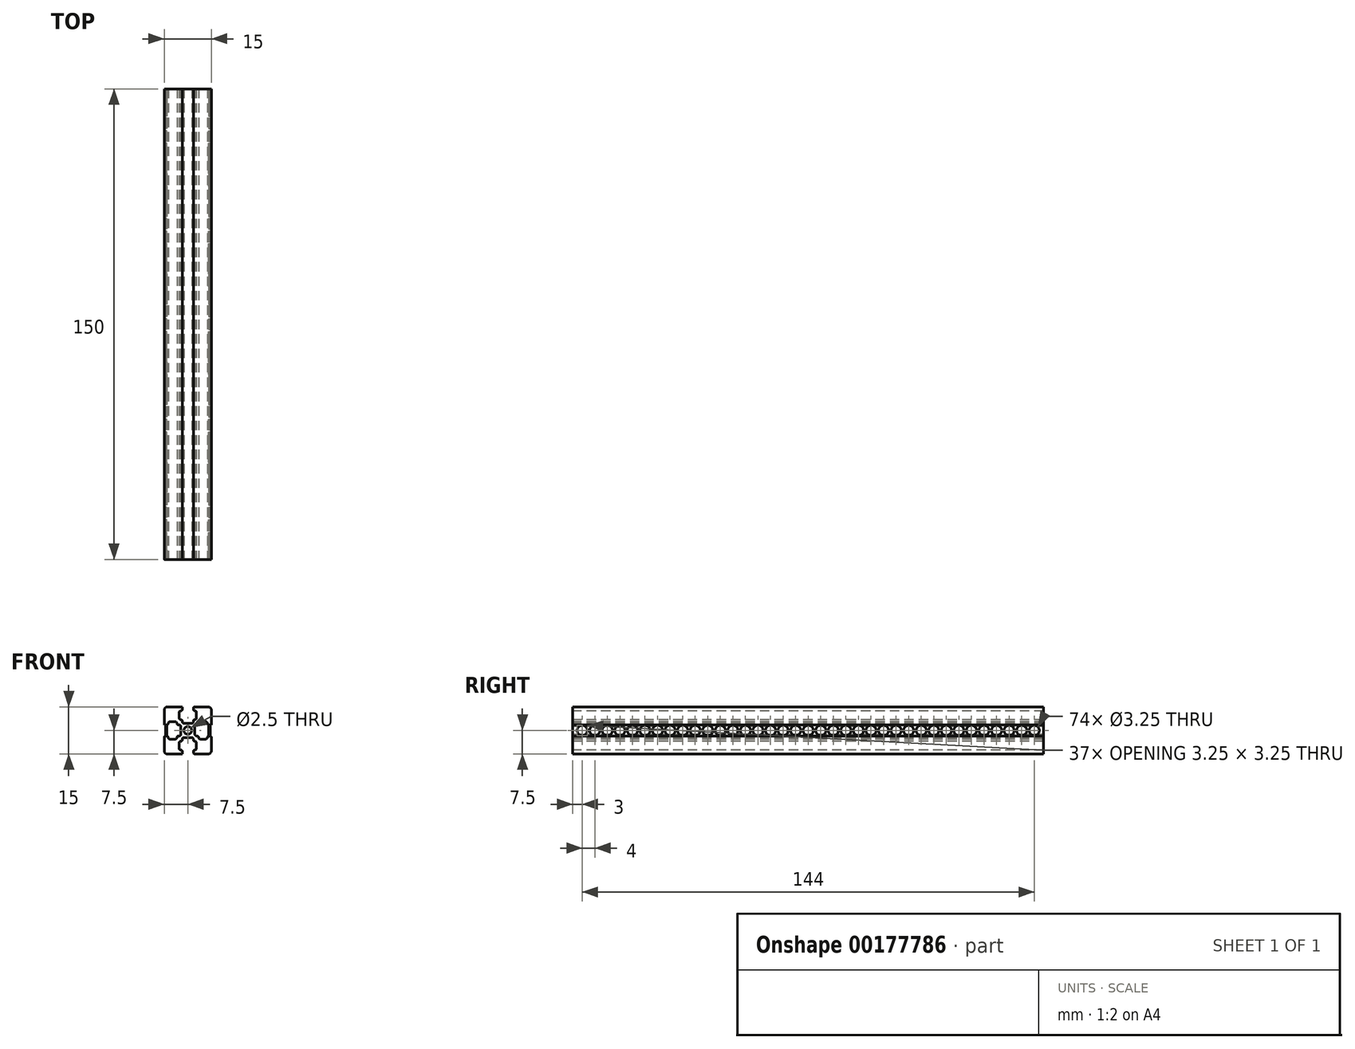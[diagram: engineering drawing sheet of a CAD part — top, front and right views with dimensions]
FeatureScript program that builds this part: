
annotation { "Feature Type Name" : "Feature", "Feature Type Description" : "" }
export const myFeature = defineFeature(function(context is Context, id is Id, definition is map)
    precondition{}
    {
        {
            var Q0;
            Q0=qCreatedBy(makeId("Front.planeOp"),FACE);
            var sketch = newSketch(context, id + "F0", { "sketchPlane" : qUnion([Q0])});
            skLineSegment(sketch, "E0.bottom", {"start": v(-6.5, 7.5) * mm, "end": v(6.5, 7.5) * mm});
            skLineSegment(sketch, "E0.top", {"start": v(-6.5, -7.5) * mm, "end": v(6.5, -7.5) * mm});
            skLineSegment(sketch, "E0.left", {"start": v(-7.5, 6.5) * mm, "end": v(-7.5, -6.5) * mm});
            skLineSegment(sketch, "E0.right", {"start": v(7.5, 6.5) * mm, "end": v(7.5, -6.5) * mm});
            skPoint(sketch, "E1.visualSharp", {"position": v(-7.5, 7.5) * mm});
            skArc(sketch, "E1.filletArc", {"start": v(-6.5, 7.5) * mm, "mid": v(-7.2, 7.2) * mm, "end": v(-7.5, 6.5) * mm});
            skPoint(sketch, "E2.visualSharp", {"position": v(7.5, 7.5) * mm});
            skArc(sketch, "E2.filletArc", {"start": v(7.5, 6.5) * mm, "mid": v(7.2, 7.2) * mm, "end": v(6.5, 7.5) * mm});
            skPoint(sketch, "E3.visualSharp", {"position": v(7.5, -7.5) * mm});
            skArc(sketch, "E3.filletArc", {"start": v(6.5, -7.5) * mm, "mid": v(7.2, -7.2) * mm, "end": v(7.5, -6.5) * mm});
            skPoint(sketch, "E4.visualSharp", {"position": v(-7.5, -7.5) * mm});
            skArc(sketch, "E4.filletArc", {"start": v(-7.5, -6.5) * mm, "mid": v(-7.2, -7.2) * mm, "end": v(-6.5, -7.5) * mm});
            skSolve(sketch);
        }
        {
            var Q0;
            Q0 = qSketchRegion(id + "F0", true);
            extrude(context, id + "F1", {"entities" : qUnion([Q0]), "depth" : 150 * mm});
        }
        {
            var Q0;
            Q0=makeQuery(id+"F1.opExtrude","CAP_FACE",FACE,{"disambiguationData":[OSD([sQuery(id+"F0.wireOp",EDGE,"E0.bottom"),sQuery(id+"F0.wireOp",EDGE,"E0.top"),sQuery(id+"F0.wireOp",EDGE,"E0.left"),sQuery(id+"F0.wireOp",EDGE,"E0.right")])],"isStart":false});
            var sketch = newSketch(context, id + "F2", { "sketchPlane" : qUnion([Q0])});
            skLineSegment(sketch, "E5.top", {"start": v(-1.25, -2.25) * mm, "end": v(1.25, -2.25) * mm});
            skLineSegment(sketch, "E5.left", {"start": v(-1.75, -7.5) * mm, "end": v(-1.75, -6.75) * mm});
            skLineSegment(sketch, "E5.right", {"start": v(1.75, -7.5) * mm, "end": v(1.75, -6.75) * mm});
            skLineSegment(sketch, "E6.bottom", {"start": v(-2.25, -3.45) * mm, "end": v(-2.25, -3.45) * mm});
            skLineSegment(sketch, "E6.top", {"start": v(-2.25, -6.25) * mm, "end": v(-2.25, -6.25) * mm});
            skLineSegment(sketch, "E6.left", {"start": v(-2.75, -3.95) * mm, "end": v(-2.75, -5.75) * mm});
            skLineSegment(sketch, "E6.right", {"start": v(2.75, -3.95) * mm, "end": v(2.75, -5.75) * mm});
            skLineSegment(sketch, "E7.trimOffspring", {"start": v(-1.75, -2.95) * mm, "end": v(-1.75, -2.75) * mm});
            skLineSegment(sketch, "E8.trimOffspring", {"start": v(2.25, -3.45) * mm, "end": v(2.25, -3.45) * mm});
            skLineSegment(sketch, "E9.trimOffspring", {"start": v(1.75, -2.95) * mm, "end": v(1.75, -2.75) * mm});
            skLineSegment(sketch, "E10.trimOffspring", {"start": v(2.25, -6.25) * mm, "end": v(2.25, -6.25) * mm});
            skLineSegment(sketch, "E11.MirrorCS", {"start": v(-1.25, 2.25) * mm, "end": v(1.25, 2.25) * mm});
            skLineSegment(sketch, "E12.MirrorCS", {"start": v(-1.75, 2.95) * mm, "end": v(-1.75, 2.75) * mm});
            skLineSegment(sketch, "E13.MirrorCS", {"start": v(1.75, 2.95) * mm, "end": v(1.75, 2.75) * mm});
            skLineSegment(sketch, "E14.MirrorCS", {"start": v(2.25, 3.45) * mm, "end": v(2.25, 3.45) * mm});
            skLineSegment(sketch, "E15.MirrorCS", {"start": v(-2.25, 3.45) * mm, "end": v(-2.25, 3.45) * mm});
            skLineSegment(sketch, "E16.MirrorCS", {"start": v(-2.75, 3.95) * mm, "end": v(-2.75, 5.75) * mm});
            skLineSegment(sketch, "E17.MirrorCS", {"start": v(2.75, 3.95) * mm, "end": v(2.75, 5.75) * mm});
            skLineSegment(sketch, "E18.MirrorCS", {"start": v(2.25, 6.25) * mm, "end": v(2.25, 6.25) * mm});
            skLineSegment(sketch, "E19.MirrorCS", {"start": v(-2.25, 6.25) * mm, "end": v(-2.25, 6.25) * mm});
            skLineSegment(sketch, "E20.MirrorCS", {"start": v(-1.75, 7.5) * mm, "end": v(-1.75, 6.75) * mm});
            skLineSegment(sketch, "E21.MirrorCS", {"start": v(1.75, 7.5) * mm, "end": v(1.75, 6.75) * mm});
            skLineSegment(sketch, "E22", {"start": v(-1.75, 7.5) * mm, "end": v(1.75, 7.5) * mm});
            skLineSegment(sketch, "E23", {"start": v(-1.75, -7.5) * mm, "end": v(1.75, -7.5) * mm});
            skPoint(sketch, "E24.visualSharp", {"position": v(-1.75, -6.25) * mm});
            skArc(sketch, "E24.filletArc", {"start": v(-1.75, -6.75) * mm, "mid": v(-1.9, -6.4) * mm, "end": v(-2.25, -6.25) * mm});
            skPoint(sketch, "E25.visualSharp", {"position": v(-2.75, -6.25) * mm});
            skArc(sketch, "E25.filletArc", {"start": v(-2.75, -5.75) * mm, "mid": v(-2.6, -6.1) * mm, "end": v(-2.25, -6.25) * mm});
            skPoint(sketch, "E26.visualSharp", {"position": v(-2.75, -3.45) * mm});
            skArc(sketch, "E26.filletArc", {"start": v(-2.25, -3.45) * mm, "mid": v(-2.6, -3.6) * mm, "end": v(-2.75, -3.95) * mm});
            skPoint(sketch, "E27.visualSharp", {"position": v(-1.75, -3.45) * mm});
            skArc(sketch, "E27.filletArc", {"start": v(-2.25, -3.45) * mm, "mid": v(-1.9, -3.3) * mm, "end": v(-1.75, -2.95) * mm});
            skPoint(sketch, "E28.visualSharp", {"position": v(1.75, -6.25) * mm});
            skArc(sketch, "E28.filletArc", {"start": v(2.25, -6.25) * mm, "mid": v(1.9, -6.4) * mm, "end": v(1.75, -6.75) * mm});
            skPoint(sketch, "E29.visualSharp", {"position": v(2.75, -6.25) * mm});
            skArc(sketch, "E29.filletArc", {"start": v(2.25, -6.25) * mm, "mid": v(2.6, -6.1) * mm, "end": v(2.75, -5.75) * mm});
            skPoint(sketch, "E30.visualSharp", {"position": v(2.75, -3.45) * mm});
            skArc(sketch, "E30.filletArc", {"start": v(2.75, -3.95) * mm, "mid": v(2.6, -3.6) * mm, "end": v(2.25, -3.45) * mm});
            skPoint(sketch, "E31.visualSharp", {"position": v(1.75, -3.45) * mm});
            skArc(sketch, "E31.filletArc", {"start": v(1.75, -2.95) * mm, "mid": v(1.9, -3.3) * mm, "end": v(2.25, -3.45) * mm});
            skPoint(sketch, "E32.visualSharp", {"position": v(1.75, -2.25) * mm});
            skArc(sketch, "E32.filletArc", {"start": v(1.75, -2.75) * mm, "mid": v(1.6, -2.4) * mm, "end": v(1.25, -2.25) * mm});
            skPoint(sketch, "E33.visualSharp", {"position": v(-1.75, -2.25) * mm});
            skArc(sketch, "E33.filletArc", {"start": v(-1.25, -2.25) * mm, "mid": v(-1.6, -2.4) * mm, "end": v(-1.75, -2.75) * mm});
            skPoint(sketch, "E34.visualSharp", {"position": v(-1.75, 2.25) * mm});
            skArc(sketch, "E34.filletArc", {"start": v(-1.75, 2.75) * mm, "mid": v(-1.6, 2.4) * mm, "end": v(-1.25, 2.25) * mm});
            skPoint(sketch, "E35.visualSharp", {"position": v(1.75, 2.25) * mm});
            skArc(sketch, "E35.filletArc", {"start": v(1.25, 2.25) * mm, "mid": v(1.6, 2.4) * mm, "end": v(1.75, 2.75) * mm});
            skPoint(sketch, "E36.visualSharp", {"position": v(1.75, 3.45) * mm});
            skArc(sketch, "E36.filletArc", {"start": v(2.25, 3.45) * mm, "mid": v(1.9, 3.3) * mm, "end": v(1.75, 2.95) * mm});
            skPoint(sketch, "E37.visualSharp", {"position": v(2.75, 6.25) * mm});
            skArc(sketch, "E37.filletArc", {"start": v(2.75, 5.75) * mm, "mid": v(2.6, 6.1) * mm, "end": v(2.25, 6.25) * mm});
            skPoint(sketch, "E38.visualSharp", {"position": v(2.75, 3.45) * mm});
            skArc(sketch, "E38.filletArc", {"start": v(2.25, 3.45) * mm, "mid": v(2.6, 3.6) * mm, "end": v(2.75, 3.95) * mm});
            skPoint(sketch, "E39.visualSharp", {"position": v(1.75, 6.25) * mm});
            skArc(sketch, "E39.filletArc", {"start": v(1.75, 6.75) * mm, "mid": v(1.9, 6.4) * mm, "end": v(2.25, 6.25) * mm});
            skPoint(sketch, "E40.visualSharp", {"position": v(-1.75, 6.25) * mm});
            skArc(sketch, "E40.filletArc", {"start": v(-2.25, 6.25) * mm, "mid": v(-1.9, 6.4) * mm, "end": v(-1.75, 6.75) * mm});
            skPoint(sketch, "E41.visualSharp", {"position": v(-1.75, 3.45) * mm});
            skArc(sketch, "E41.filletArc", {"start": v(-1.75, 2.95) * mm, "mid": v(-1.9, 3.3) * mm, "end": v(-2.25, 3.45) * mm});
            skPoint(sketch, "E42.visualSharp", {"position": v(-2.75, 3.45) * mm});
            skArc(sketch, "E42.filletArc", {"start": v(-2.75, 3.95) * mm, "mid": v(-2.6, 3.6) * mm, "end": v(-2.25, 3.45) * mm});
            skPoint(sketch, "E43.visualSharp", {"position": v(-2.75, 6.25) * mm});
            skArc(sketch, "E43.filletArc", {"start": v(-2.25, 6.25) * mm, "mid": v(-2.6, 6.1) * mm, "end": v(-2.75, 5.75) * mm});
            skSolve(sketch);
        }
        {
            var Q0;
            Q0 = qSketchRegion(id + "F2", true);
            extrude(context, id + "F3", {"entities" : qUnion([Q0]), "operationType" : NewBodyOperationType.REMOVE, "endBound" : BoundingType.THROUGH_ALL, "oppositeDirection" : true, "depth" : 25.4 * mm});
        }
        {
            var Q0;
            Q0=makeQuery(id+"F1.opExtrude","CAP_FACE",FACE,{"disambiguationData":[OSD([sQuery(id+"F0.wireOp",EDGE,"E0.bottom"),sQuery(id+"F0.wireOp",EDGE,"E0.top"),sQuery(id+"F0.wireOp",EDGE,"E0.left"),sQuery(id+"F0.wireOp",EDGE,"E0.right")])],"isStart":false});
            var sketch = newSketch(context, id + "F4", { "sketchPlane" : qUnion([Q0])});
            skLineSegment(sketch, "E44.bottom", {"start": v(7.5, 1.75) * mm, "end": v(6.75, 1.75) * mm});
            skLineSegment(sketch, "E44.top", {"start": v(7.5, -1.75) * mm, "end": v(6.75, -1.75) * mm});
            skLineSegment(sketch, "E44.left", {"start": v(7.5, 1.75) * mm, "end": v(7.5, -1.75) * mm});
            skLineSegment(sketch, "E44.right", {"start": v(2.25, 1.25) * mm, "end": v(2.25, -1.25) * mm});
            skLineSegment(sketch, "E45.bottom", {"start": v(3.95, 2.75) * mm, "end": v(5.75, 2.75) * mm});
            skLineSegment(sketch, "E45.top", {"start": v(3.95, -2.75) * mm, "end": v(5.75, -2.75) * mm});
            skLineSegment(sketch, "E45.left", {"start": v(3.45, 2.25) * mm, "end": v(3.45, 2.25) * mm});
            skLineSegment(sketch, "E45.right", {"start": v(6.25, 2.25) * mm, "end": v(6.25, 2.25) * mm});
            skLineSegment(sketch, "E46.trimOffspring", {"start": v(2.95, 1.75) * mm, "end": v(2.75, 1.75) * mm});
            skLineSegment(sketch, "E47.trimOffspring", {"start": v(3.45, -2.25) * mm, "end": v(3.45, -2.25) * mm});
            skLineSegment(sketch, "E48.trimOffspring", {"start": v(6.25, -2.25) * mm, "end": v(6.25, -2.25) * mm});
            skLineSegment(sketch, "E49.trimOffspring", {"start": v(2.95, -1.75) * mm, "end": v(2.75, -1.75) * mm});
            skLineSegment(sketch, "E50.MirrorCS", {"start": v(-2.25, 1.25) * mm, "end": v(-2.25, -1.25) * mm});
            skLineSegment(sketch, "E51.MirrorCS", {"start": v(-2.95, 1.75) * mm, "end": v(-2.75, 1.75) * mm});
            skLineSegment(sketch, "E52.MirrorCS", {"start": v(-2.95, -1.75) * mm, "end": v(-2.75, -1.75) * mm});
            skLineSegment(sketch, "E53.MirrorCS", {"start": v(-3.45, -2.25) * mm, "end": v(-3.45, -2.25) * mm});
            skLineSegment(sketch, "E54.MirrorCS", {"start": v(-3.95, -2.75) * mm, "end": v(-5.75, -2.75) * mm});
            skLineSegment(sketch, "E55.MirrorCS", {"start": v(-6.25, -2.25) * mm, "end": v(-6.25, -2.25) * mm});
            skLineSegment(sketch, "E56.MirrorCS", {"start": v(-7.5, -1.75) * mm, "end": v(-6.75, -1.75) * mm});
            skLineSegment(sketch, "E57.MirrorCS", {"start": v(-7.5, 1.75) * mm, "end": v(-7.5, -1.75) * mm});
            skLineSegment(sketch, "E58.MirrorCS", {"start": v(-7.5, 1.75) * mm, "end": v(-6.75, 1.75) * mm});
            skLineSegment(sketch, "E59.MirrorCS", {"start": v(-6.25, 2.25) * mm, "end": v(-6.25, 2.25) * mm});
            skLineSegment(sketch, "E60.MirrorCS", {"start": v(-3.95, 2.75) * mm, "end": v(-5.75, 2.75) * mm});
            skLineSegment(sketch, "E61.MirrorCS", {"start": v(-3.45, 2.25) * mm, "end": v(-3.45, 2.25) * mm});
            skPoint(sketch, "E62.visualSharp", {"position": v(6.25, 1.75) * mm});
            skArc(sketch, "E62.filletArc", {"start": v(6.25, 2.25) * mm, "mid": v(6.4, 1.9) * mm, "end": v(6.75, 1.75) * mm});
            skPoint(sketch, "E63.visualSharp", {"position": v(6.25, 2.75) * mm});
            skArc(sketch, "E63.filletArc", {"start": v(6.25, 2.25) * mm, "mid": v(6.1, 2.6) * mm, "end": v(5.75, 2.75) * mm});
            skPoint(sketch, "E64.visualSharp", {"position": v(3.45, 2.75) * mm});
            skArc(sketch, "E64.filletArc", {"start": v(3.95, 2.75) * mm, "mid": v(3.6, 2.6) * mm, "end": v(3.45, 2.25) * mm});
            skPoint(sketch, "E65.visualSharp", {"position": v(3.45, 1.75) * mm});
            skArc(sketch, "E65.filletArc", {"start": v(2.95, 1.75) * mm, "mid": v(3.3, 1.9) * mm, "end": v(3.45, 2.25) * mm});
            skPoint(sketch, "E66.visualSharp", {"position": v(2.25, 1.75) * mm});
            skArc(sketch, "E66.filletArc", {"start": v(2.75, 1.75) * mm, "mid": v(2.4, 1.6) * mm, "end": v(2.25, 1.25) * mm});
            skPoint(sketch, "E67.visualSharp", {"position": v(2.25, -1.75) * mm});
            skArc(sketch, "E67.filletArc", {"start": v(2.25, -1.25) * mm, "mid": v(2.4, -1.6) * mm, "end": v(2.75, -1.75) * mm});
            skPoint(sketch, "E68.visualSharp", {"position": v(3.45, -1.75) * mm});
            skArc(sketch, "E68.filletArc", {"start": v(3.45, -2.25) * mm, "mid": v(3.3, -1.9) * mm, "end": v(2.95, -1.75) * mm});
            skPoint(sketch, "E69.visualSharp", {"position": v(3.45, -2.75) * mm});
            skArc(sketch, "E69.filletArc", {"start": v(3.45, -2.25) * mm, "mid": v(3.6, -2.6) * mm, "end": v(3.95, -2.75) * mm});
            skPoint(sketch, "E70.visualSharp", {"position": v(6.25, -2.75) * mm});
            skArc(sketch, "E70.filletArc", {"start": v(5.75, -2.75) * mm, "mid": v(6.1, -2.6) * mm, "end": v(6.25, -2.25) * mm});
            skPoint(sketch, "E71.visualSharp", {"position": v(6.25, -1.75) * mm});
            skArc(sketch, "E71.filletArc", {"start": v(6.75, -1.75) * mm, "mid": v(6.4, -1.9) * mm, "end": v(6.25, -2.25) * mm});
            skPoint(sketch, "E72.visualSharp", {"position": v(-2.25, 1.75) * mm});
            skArc(sketch, "E72.filletArc", {"start": v(-2.25, 1.25) * mm, "mid": v(-2.4, 1.6) * mm, "end": v(-2.75, 1.75) * mm});
            skPoint(sketch, "E73.visualSharp", {"position": v(-2.25, -1.75) * mm});
            skArc(sketch, "E73.filletArc", {"start": v(-2.75, -1.75) * mm, "mid": v(-2.4, -1.6) * mm, "end": v(-2.25, -1.25) * mm});
            skPoint(sketch, "E74.visualSharp", {"position": v(-3.45, -1.75) * mm});
            skArc(sketch, "E74.filletArc", {"start": v(-2.95, -1.75) * mm, "mid": v(-3.3, -1.9) * mm, "end": v(-3.45, -2.25) * mm});
            skPoint(sketch, "E75.visualSharp", {"position": v(-3.45, -2.75) * mm});
            skArc(sketch, "E75.filletArc", {"start": v(-3.95, -2.75) * mm, "mid": v(-3.6, -2.6) * mm, "end": v(-3.45, -2.25) * mm});
            skPoint(sketch, "E76.visualSharp", {"position": v(-6.25, -2.75) * mm});
            skArc(sketch, "E76.filletArc", {"start": v(-6.25, -2.25) * mm, "mid": v(-6.1, -2.6) * mm, "end": v(-5.75, -2.75) * mm});
            skPoint(sketch, "E77.visualSharp", {"position": v(-6.25, -1.75) * mm});
            skArc(sketch, "E77.filletArc", {"start": v(-6.25, -2.25) * mm, "mid": v(-6.4, -1.9) * mm, "end": v(-6.75, -1.75) * mm});
            skPoint(sketch, "E78.visualSharp", {"position": v(-6.25, 1.75) * mm});
            skArc(sketch, "E78.filletArc", {"start": v(-6.75, 1.75) * mm, "mid": v(-6.4, 1.9) * mm, "end": v(-6.25, 2.25) * mm});
            skPoint(sketch, "E79.visualSharp", {"position": v(-6.25, 2.75) * mm});
            skArc(sketch, "E79.filletArc", {"start": v(-5.75, 2.75) * mm, "mid": v(-6.1, 2.6) * mm, "end": v(-6.25, 2.25) * mm});
            skPoint(sketch, "E80.visualSharp", {"position": v(-3.45, 2.75) * mm});
            skArc(sketch, "E80.filletArc", {"start": v(-3.45, 2.25) * mm, "mid": v(-3.6, 2.6) * mm, "end": v(-3.95, 2.75) * mm});
            skPoint(sketch, "E81.visualSharp", {"position": v(-3.45, 1.75) * mm});
            skArc(sketch, "E81.filletArc", {"start": v(-3.45, 2.25) * mm, "mid": v(-3.3, 1.9) * mm, "end": v(-2.95, 1.75) * mm});
            skSolve(sketch);
        }
        {
            var Q0;
            Q0 = qSketchRegion(id + "F4", true);
            extrude(context, id + "F5", {"entities" : qUnion([Q0]), "operationType" : NewBodyOperationType.REMOVE, "endBound" : BoundingType.THROUGH_ALL, "oppositeDirection" : true, "depth" : 25.4 * mm});
        }
        {
            var Q0;
            Q0=makeQuery(id+"F1.opExtrude","CAP_FACE",FACE,{"disambiguationData":[OSD([sQuery(id+"F0.wireOp",EDGE,"E0.bottom"),sQuery(id+"F0.wireOp",EDGE,"E0.top"),sQuery(id+"F0.wireOp",EDGE,"E0.left"),sQuery(id+"F0.wireOp",EDGE,"E0.right")])],"isStart":false});
            var sketch = newSketch(context, id + "F6", { "sketchPlane" : qUnion([Q0])});
            skCircle(sketch, "E82", {"center": v(0, 0) * mm, "radius": 1.25 * mm});
            skSolve(sketch);
        }
        {
            var Q0;
            Q0 = qSketchRegion(id + "F6", true);
            extrude(context, id + "F7", {"entities" : qUnion([Q0]), "operationType" : NewBodyOperationType.REMOVE, "endBound" : BoundingType.THROUGH_ALL, "oppositeDirection" : true, "depth" : 25.4 * mm});
        }
        {
            var Q0;
            Q0=makeQuery(id+"F3.boolean.opBoolean","COPY",EDGE,{"derivedFrom":makeQuery(id+"F3.opExtrude","SWEPT_EDGE",EDGE,{"disambiguationData":[OSD([sQuery(id+"F0.wireOp",EDGE,"E0.top"),sQuery(id+"F2.wireOp",EDGE,"E5.left"),sQuery(id+"F2.wireOp",EDGE,"E23")])]})});
            var Q1;
            Q1=makeQuery(id+"F5.boolean.opBoolean","COPY",EDGE,{"derivedFrom":makeQuery(id+"F5.opExtrude","SWEPT_EDGE",EDGE,{"disambiguationData":[OSD([sQuery(id+"F0.wireOp",EDGE,"E0.right"),sQuery(id+"F4.wireOp",EDGE,"E44.bottom"),sQuery(id+"F4.wireOp",EDGE,"E44.left")])]})});
            var Q2;
            Q2=makeQuery(id+"F5.boolean.opBoolean","COPY",EDGE,{"derivedFrom":makeQuery(id+"F5.opExtrude","SWEPT_EDGE",EDGE,{"disambiguationData":[OSD([sQuery(id+"F0.wireOp",EDGE,"E0.left"),sQuery(id+"F4.wireOp",EDGE,"E57.MirrorCS"),sQuery(id+"F4.wireOp",EDGE,"E58.MirrorCS")])]})});
            var Q3;
            Q3=makeQuery(id+"F3.boolean.opBoolean","COPY",EDGE,{"derivedFrom":makeQuery(id+"F3.opExtrude","SWEPT_EDGE",EDGE,{"disambiguationData":[OSD([sQuery(id+"F0.wireOp",EDGE,"E0.bottom"),sQuery(id+"F2.wireOp",EDGE,"E21.MirrorCS"),sQuery(id+"F2.wireOp",EDGE,"E22")])]})});
            var Q4;
            Q4=makeQuery(id+"F3.boolean.opBoolean","COPY",EDGE,{"derivedFrom":makeQuery(id+"F3.opExtrude","SWEPT_EDGE",EDGE,{"disambiguationData":[OSD([sQuery(id+"F0.wireOp",EDGE,"E0.top"),sQuery(id+"F2.wireOp",EDGE,"E5.right"),sQuery(id+"F2.wireOp",EDGE,"E23")])]})});
            var Q5;
            Q5=makeQuery(id+"F5.boolean.opBoolean","COPY",EDGE,{"derivedFrom":makeQuery(id+"F5.opExtrude","SWEPT_EDGE",EDGE,{"disambiguationData":[OSD([sQuery(id+"F0.wireOp",EDGE,"E0.left"),sQuery(id+"F4.wireOp",EDGE,"E56.MirrorCS"),sQuery(id+"F4.wireOp",EDGE,"E57.MirrorCS")])]})});
            var Q6;
            Q6=makeQuery(id+"F5.boolean.opBoolean","COPY",EDGE,{"derivedFrom":makeQuery(id+"F5.opExtrude","SWEPT_EDGE",EDGE,{"disambiguationData":[OSD([sQuery(id+"F0.wireOp",EDGE,"E0.right"),sQuery(id+"F4.wireOp",EDGE,"E44.top"),sQuery(id+"F4.wireOp",EDGE,"E44.left")])]})});
            var Q7;
            Q7=makeQuery(id+"F3.boolean.opBoolean","COPY",EDGE,{"derivedFrom":makeQuery(id+"F3.opExtrude","SWEPT_EDGE",EDGE,{"disambiguationData":[OSD([sQuery(id+"F0.wireOp",EDGE,"E0.bottom"),sQuery(id+"F2.wireOp",EDGE,"E20.MirrorCS"),sQuery(id+"F2.wireOp",EDGE,"E22")])]})});
            fillet(context, id + "F8", {"entities" : qUnion([Q0, Q1, Q2, Q3, Q4, Q5, Q6, Q7]), "radius" : 0.5 * mm, "tangentPropagation" : true, "allowEdgeOverflow" : false});
        }
        {
            var Q0;
            Q0=makeQuery(id+"F1.opExtrude","CAP_FACE",FACE,{"disambiguationData":[OSD([sQuery(id+"F0.wireOp",EDGE,"E0.bottom"),sQuery(id+"F0.wireOp",EDGE,"E0.top"),sQuery(id+"F0.wireOp",EDGE,"E0.left"),sQuery(id+"F0.wireOp",EDGE,"E0.right"),sQuery(id+"F0.wireOp",EDGE,"E1.filletArc"),sQuery(id+"F0.wireOp",EDGE,"E2.filletArc"),sQuery(id+"F0.wireOp",EDGE,"E3.filletArc"),sQuery(id+"F0.wireOp",EDGE,"E4.filletArc")])],"isStart":false});
            var sketch = newSketch(context, id + "F9", { "sketchPlane" : qUnion([Q0])});
            skLineSegment(sketch, "E83.bottom", {"start": v(6.65, 1.75) * mm, "end": v(7.1, 1.75) * mm});
            skLineSegment(sketch, "E83.top", {"start": v(6.65, -1.75) * mm, "end": v(7.1, -1.75) * mm});
            skLineSegment(sketch, "E83.left", {"start": v(6.65, 1.75) * mm, "end": v(6.65, -1.75) * mm});
            skLineSegment(sketch, "E83.right", {"start": v(7.1, 1.75) * mm, "end": v(7.1, -1.75) * mm});
            skSolve(sketch);
        }
        {
            var Q0;
            Q0 = qSketchRegion(id + "F9", true);
            var Q1;
            Q1=makeQuery(id+"F1.opExtrude","CAP_FACE",FACE,{"disambiguationData":[OSD([sQuery(id+"F0.wireOp",EDGE,"E0.bottom"),sQuery(id+"F0.wireOp",EDGE,"E0.top"),sQuery(id+"F0.wireOp",EDGE,"E0.left"),sQuery(id+"F0.wireOp",EDGE,"E0.right"),sQuery(id+"F0.wireOp",EDGE,"E1.filletArc"),sQuery(id+"F0.wireOp",EDGE,"E2.filletArc"),sQuery(id+"F0.wireOp",EDGE,"E3.filletArc"),sQuery(id+"F0.wireOp",EDGE,"E4.filletArc")])],"isStart":true});
            extrude(context, id + "F10", {"entities" : qUnion([Q0]), "endBound" : BoundingType.UP_TO_SURFACE, "oppositeDirection" : true, "endBoundEntityFace" : qUnion([Q1]), "depth" : 25.4 * mm});
        }
        {
            var Q0;
            Q0=makeQuery(id+"F10.opExtrude","SWEPT_FACE",FACE,{"disambiguationData":[OSD([sQuery(id+"F9.wireOp",EDGE,"E83.right")])]});
            var sketch = newSketch(context, id + "F11", { "sketchPlane" : qUnion([Q0])});
            skCircle(sketch, "E84", {"center": v(-3, 0) * mm, "radius": 1.62 * mm});
            skCircle(sketch, "E85.1.0.0", {"center": v(-7, 0) * mm, "radius": 1.62 * mm});
            skCircle(sketch, "E85.2.0.0", {"center": v(-11, 0) * mm, "radius": 1.62 * mm});
            skCircle(sketch, "E85.3.0.0", {"center": v(-15, 0) * mm, "radius": 1.62 * mm});
            skCircle(sketch, "E85.4.0.0", {"center": v(-19, 0) * mm, "radius": 1.62 * mm});
            skCircle(sketch, "E85.5.0.0", {"center": v(-23, 0) * mm, "radius": 1.62 * mm});
            skCircle(sketch, "E85.6.0.0", {"center": v(-27, 0) * mm, "radius": 1.62 * mm});
            skLineSegment(sketch, "E85.direction1", {"start": v(-3, 0) * mm, "end": v(-7, 0) * mm, "construction": true});
            skCircle(sketch, "E86.0.7.0", {"center": v(-31, 0) * mm, "radius": 1.62 * mm});
            skCircle(sketch, "E86.0.8.0", {"center": v(-35, 0) * mm, "radius": 1.62 * mm});
            skCircle(sketch, "E86.0.9.0", {"center": v(-39, 0) * mm, "radius": 1.62 * mm});
            skCircle(sketch, "E86.0.10.0", {"center": v(-43, 0) * mm, "radius": 1.62 * mm});
            skCircle(sketch, "E86.0.11.0", {"center": v(-47, 0) * mm, "radius": 1.62 * mm});
            skCircle(sketch, "E86.0.12.0", {"center": v(-51, 0) * mm, "radius": 1.62 * mm});
            skCircle(sketch, "E86.0.13.0", {"center": v(-55, 0) * mm, "radius": 1.62 * mm});
            skCircle(sketch, "E86.0.14.0", {"center": v(-59, 0) * mm, "radius": 1.62 * mm});
            skCircle(sketch, "E86.0.15.0", {"center": v(-63, 0) * mm, "radius": 1.62 * mm});
            skCircle(sketch, "E86.0.16.0", {"center": v(-67, 0) * mm, "radius": 1.62 * mm});
            skCircle(sketch, "E86.0.17.0", {"center": v(-71, 0) * mm, "radius": 1.62 * mm});
            skCircle(sketch, "E86.0.18.0", {"center": v(-75, 0) * mm, "radius": 1.62 * mm});
            skCircle(sketch, "E86.0.19.0", {"center": v(-79, 0) * mm, "radius": 1.62 * mm});
            skCircle(sketch, "E86.0.20.0", {"center": v(-83, 0) * mm, "radius": 1.62 * mm});
            skCircle(sketch, "E86.0.21.0", {"center": v(-87, 0) * mm, "radius": 1.62 * mm});
            skCircle(sketch, "E86.0.22.0", {"center": v(-91, 0) * mm, "radius": 1.62 * mm});
            skCircle(sketch, "E86.0.23.0", {"center": v(-95, 0) * mm, "radius": 1.62 * mm});
            skCircle(sketch, "E86.0.24.0", {"center": v(-99, 0) * mm, "radius": 1.62 * mm});
            skCircle(sketch, "E86.0.25.0", {"center": v(-103, 0) * mm, "radius": 1.62 * mm});
            skCircle(sketch, "E86.0.26.0", {"center": v(-107, 0) * mm, "radius": 1.62 * mm});
            skCircle(sketch, "E86.0.27.0", {"center": v(-111, 0) * mm, "radius": 1.62 * mm});
            skCircle(sketch, "E86.0.28.0", {"center": v(-115, 0) * mm, "radius": 1.62 * mm});
            skCircle(sketch, "E86.0.29.0", {"center": v(-119, 0) * mm, "radius": 1.62 * mm});
            skCircle(sketch, "E87.0.30.0", {"center": v(-123, 0) * mm, "radius": 1.62 * mm});
            skCircle(sketch, "E87.0.31.0", {"center": v(-127, 0) * mm, "radius": 1.62 * mm});
            skCircle(sketch, "E87.0.32.0", {"center": v(-131, 0) * mm, "radius": 1.62 * mm});
            skCircle(sketch, "E87.0.33.0", {"center": v(-135, 0) * mm, "radius": 1.62 * mm});
            skCircle(sketch, "E87.0.34.0", {"center": v(-139, 0) * mm, "radius": 1.62 * mm});
            skCircle(sketch, "E88.0.35.0", {"center": v(-143, 0) * mm, "radius": 1.62 * mm});
            skCircle(sketch, "E88.0.36.0", {"center": v(-147, 0) * mm, "radius": 1.62 * mm});
            skSolve(sketch);
        }
        {
            var Q0;
            Q0 = qSketchRegion(id + "F11", true);
            extrude(context, id + "F12", {"entities" : qUnion([Q0]), "operationType" : NewBodyOperationType.REMOVE, "oppositeDirection" : true, "depth" : 1 * mm});
        }
        {
            var Q0;
            Q0=makeQuery(id+"F10.opExtrude","SWEPT_BODY",BODY,{"disambiguationData":[OSD([sQuery(id+"F9.wireOp",EDGE,"E83.bottom"),sQuery(id+"F9.wireOp",EDGE,"E83.top"),sQuery(id+"F9.wireOp",EDGE,"E83.left"),sQuery(id+"F9.wireOp",EDGE,"E83.right")])]});
            var Q1;
            Q1=qCreatedBy(makeId("Right.planeOp"),FACE);
            mirror(context, id + "F13", {"entities" : qUnion([Q0]), "mirrorPlane" : qUnion([Q1])});
        }
    });
